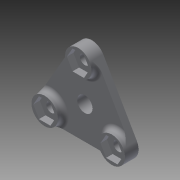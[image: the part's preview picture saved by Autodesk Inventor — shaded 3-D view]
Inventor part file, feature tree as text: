
AUTODESK INVENTOR PART (.ipt)
format: ipt  version: 2013 (Build 170138000, 138)  size: 190,976 bytes
history: native  units: in
note: dims shown in document units (in); Inventor stores cm internally (conversion verified against a paired STEP export)
features: extrude x3, sketch x3, fillet x2
ambient origin geometry x8: Origin, YZ Plane, XZ Plane, XY Plane, X Axis, Y Axis, Z Axis, Center Point
bodies: Solid1 (feature_tree)
feature tree (8):
  extrude  "Extrusion1"  Depth=0.1772in
  extrude  "Extrusion2"  Depth=0.2756in
  fillet  "Fillet1"  Radius=0.4724in
  extrude  "Extrusion4"  Depth=0.2362in
  fillet  "Fillet3"  Radius=0.125in
  sketch  "Sketch1"  dims[d7=1.2008in d8=0.1772in]
  sketch  "Sketch2"  dims[d9=1.1811in d11=360.0deg d13=0.2756in d14=0.4724in]
  sketch  "Sketch4"  dims[d15=1.1811in d17=360.0deg d19=0.2362in d20=0.125in d21=0.0in d22=0.5118in d23=0.1772in d24=0.0in d25=0.1181in d31=0.3543in d32=0.3543in d33=0.3543in d34=0.1181in d35=0.0in d36=0.0787in]
